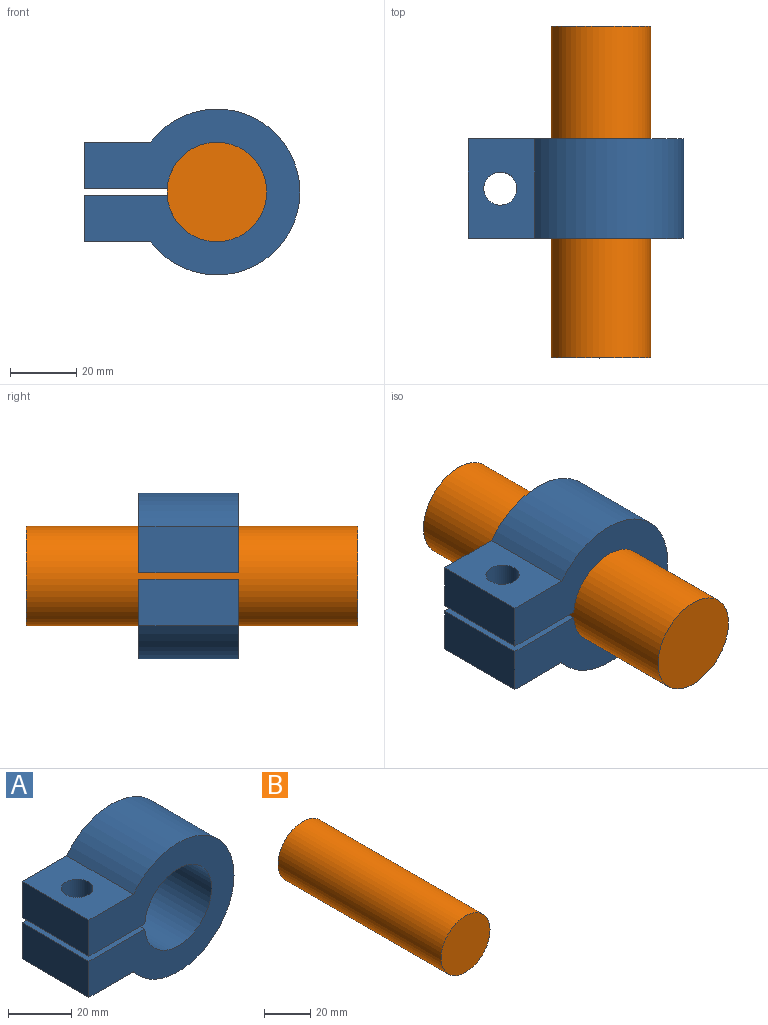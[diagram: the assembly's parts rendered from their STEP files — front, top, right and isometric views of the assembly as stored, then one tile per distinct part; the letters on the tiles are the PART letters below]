
ASSEMBLY  parts=2 mates=1
PART A: 12 faces, bbox 65x30x50 mm
  f0: plane 30x25.03mm, normal (0,0,-1), area 672.5mm2, adj f1,f7,f8,f9,f11
  f1: cylinder r=15mm len=30mm, axis (0,1,0), area 2767.4mm2, adj f0,f2,f8,f9
  f2: plane 30x25.03mm, normal (0,0,1), area 672.5mm2, adj f1,f3,f8,f9,f10
  f3: plane 30x14mm, normal (-1,0,0), area 420mm2, adj f2,f4,f8,f9
  f4: plane 30x20mm, normal (0,0,-1), area 521.5mm2, adj f3,f5,f8,f9,f10
  f5: cylinder r=25mm len=50mm, axis (0,1,0), area 3747.1mm2, adj f4,f6,f8,f9
  f6: plane 30x20mm, normal (0,0,1), area 521.5mm2, adj f5,f7,f8,f9,f11
  f7: plane 30x14mm, normal (-1,0,0), area 420mm2, adj f0,f6,f8,f9
  f8: plane 65x50mm, normal (0,-1,0), area 1704.4mm2, adj f0,f1,f2,f3,f4,f5,f6,f7
  f9: plane 65x50mm, normal (0,1,0), area 1704.4mm2, adj f0,f1,f2,f3,f4,f5,f6,f7
  f10: cylinder r=5mm len=14mm, axis (0,0,1), area 439.8mm2, adj f2,f4
  f11: cylinder r=5mm len=14mm, axis (0,0,1), area 439.8mm2, adj f0,f6
PART B: 3 faces, bbox 30x100x30 mm
  f0: cylinder r=15mm len=100mm, axis (0,1,0), area 9424.8mm2, adj f1,f2
  f1: plane 30x30mm, normal (0,-1,0), area 706.9mm2, adj f0
  f2: plane 30x30mm, normal (0,1,0), area 706.9mm2, adj f0
PLACE A t=(-26.4,-6.24,-2.5)mm
PLACE B t=(-26.4,27.76,-2.5)mm
MATE cylindrical B.f0 <-> A.f1  axis (0,1,0) through (-26.4,-22.24,-2.5)mm
